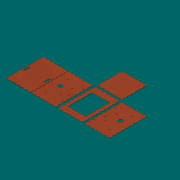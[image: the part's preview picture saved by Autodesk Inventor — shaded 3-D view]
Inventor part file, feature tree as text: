
AUTODESK INVENTOR PART (.ipt)
format: ipt  version: 2016 SP2 (Build 200236200, 236)  size: 920,576 bytes
history: native  units: mm
features: reference x5, other x1, extrude x1, sketch x1
ambient origin geometry x8: Origin, YZ Plane, XZ Plane, XY Plane, X Axis, Y Axis, Z Axis, Center Point
bodies: Body1 (feature_tree)
feature tree (8):
  other  "<userpath>\oneDrive\projects\splitFlapDisplay\parameters.xlsx"
  extrude  "Extrusion2"  Depth=3.175mm
  sketch  "Sketch2"  dims[d8=0.1mm d9=0.1mm d10=0.1mm d11=0.1mm d12=0.1mm d13=0.1mm d14=0.1mm d15=0.1mm d16=3.175mm d17=0.0mm]
  reference  "Reference6"
  reference  "Reference7"
  reference  "Reference8"
  reference  "Reference9"
  reference  "Reference10"
